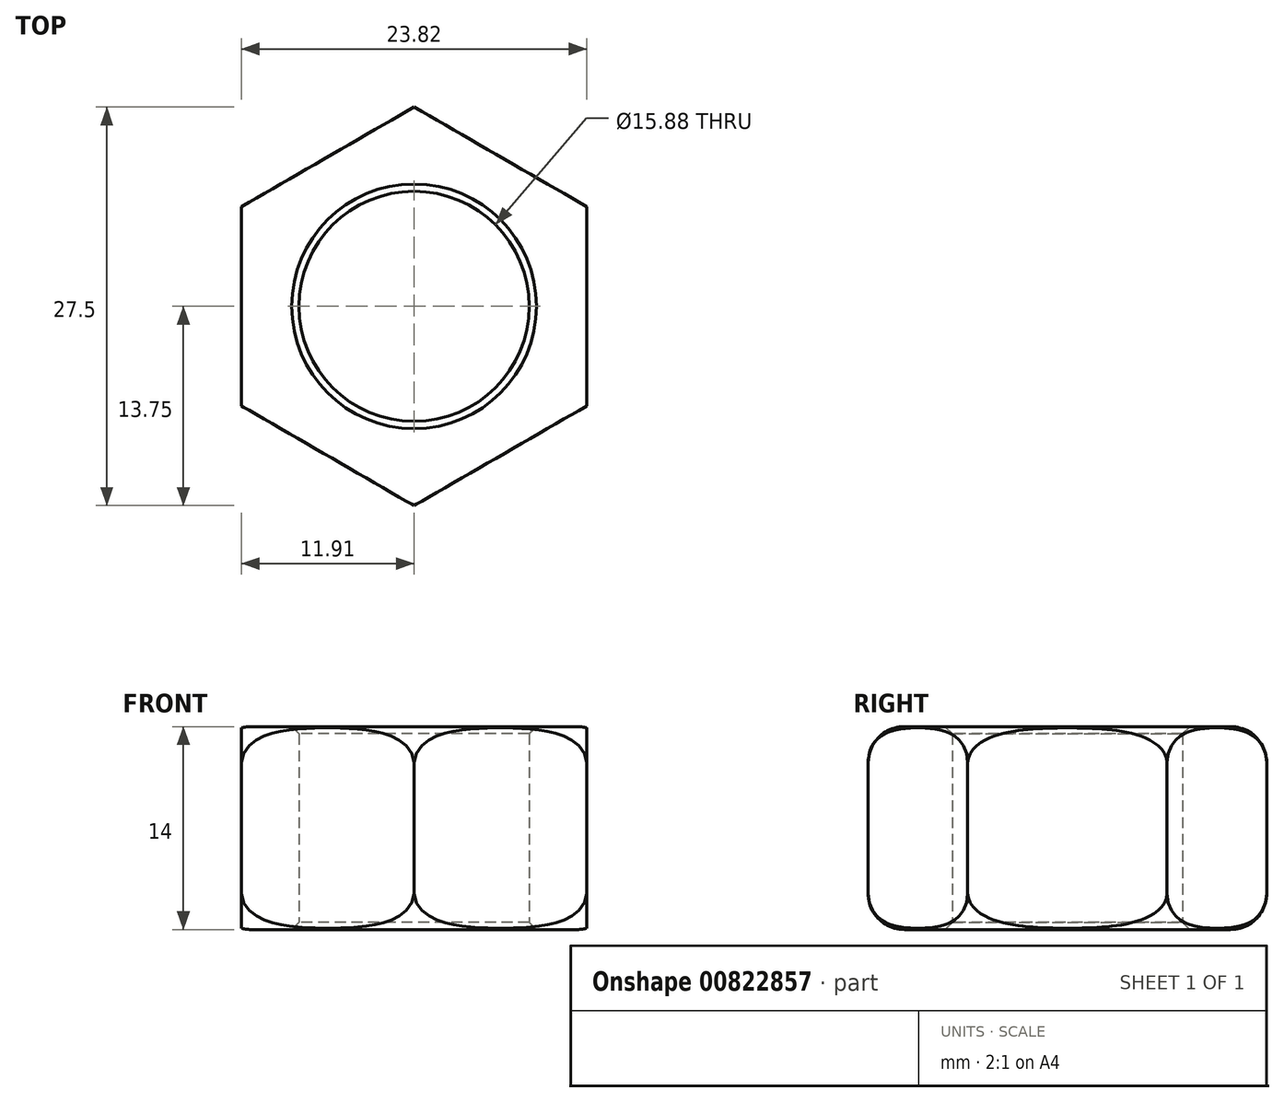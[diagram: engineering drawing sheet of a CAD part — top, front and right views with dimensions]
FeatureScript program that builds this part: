
annotation { "Feature Type Name" : "Feature", "Feature Type Description" : "" }
export const myFeature = defineFeature(function(context is Context, id is Id, definition is map)
    precondition{}
    {
        {
            var Q0;
            Q0=qCreatedBy(makeId("Top.planeOp"),FACE);
            var sketch = newSketch(context, id + "F0", { "sketchPlane" : qUnion([Q0])});
            skLineSegment(sketch, "E0", {"start": v(0, 0) * mm, "end": v(11.9, 0) * mm, "construction": true});
            skCircle(sketch, "E1.cCircle", {"center": v(0, 0) * mm, "radius": 11.9 * mm, "construction": true});
            skLineSegment(sketch, "E1.0", {"start": v(11.9, 6.87) * mm, "end": v(11.9, -6.87) * mm, "construction": true});
            skLineSegment(sketch, "E1.1", {"start": v(11.9, -6.87) * mm, "end": v(0, -13.75) * mm, "construction": true});
            skLineSegment(sketch, "E1.2", {"start": v(0, -13.75) * mm, "end": v(-11.9, -6.87) * mm, "construction": true});
            skLineSegment(sketch, "E1.3", {"start": v(-11.9, -6.87) * mm, "end": v(-11.9, 6.87) * mm, "construction": true});
            skLineSegment(sketch, "E1.4", {"start": v(-11.9, 6.87) * mm, "end": v(0, 13.75) * mm, "construction": true});
            skLineSegment(sketch, "E1.5", {"start": v(0, 13.75) * mm, "end": v(11.9, 6.87) * mm, "construction": true});
            skPoint(sketch, "E1.0.midPoint", {"position": v(11.9, 0) * mm});
            skCircle(sketch, "E2", {"center": v(0, 0) * mm, "radius": 13.75 * mm});
            skCircle(sketch, "E3", {"center": v(0, 0) * mm, "radius": 7.94 * mm});
            skSolve(sketch);
        }
        {
            var Q0;
            Q0 = qSketchRegion(id + "F0", true);
            extrude(context, id + "F1", {"entities" : qUnion([Q0]), "depth" : 14 * mm, "offsetDistance" : 25 * mm});
        }
        {
            var Q0;
            Q0=makeQuery(id+"F1.opExtrude","CAP_FACE",FACE,{"disambiguationData":[OSD([sQuery(id+"F0.wireOp",EDGE,"E2"),sQuery(id+"F0.wireOp",EDGE,"E3")])],"isStart":false});
            var sketch = newSketch(context, id + "F2", { "sketchPlane" : qUnion([Q0])});
            skLineSegment(sketch, "E4.0", {"start": v(0, 13.75) * mm, "end": v(11.9, 6.87) * mm});
            skLineSegment(sketch, "E5.0", {"start": v(-11.9, 6.87) * mm, "end": v(0, 13.75) * mm});
            skLineSegment(sketch, "E6.0", {"start": v(-11.9, -6.87) * mm, "end": v(-11.9, 6.87) * mm});
            skLineSegment(sketch, "E7.0", {"start": v(0, -13.75) * mm, "end": v(-11.9, -6.87) * mm});
            skLineSegment(sketch, "E8.0", {"start": v(11.9, -6.87) * mm, "end": v(0, -13.75) * mm});
            skLineSegment(sketch, "E9.0", {"start": v(11.9, 6.87) * mm, "end": v(11.9, -6.87) * mm});
            skCircle(sketch, "E10", {"center": v(0, 0) * mm, "radius": 16.81 * mm});
            skSolve(sketch);
        }
        {
            var Q0;
            Q0=makeQuery(id+"F1.opExtrude","CAP_EDGE",EDGE,{"disambiguationData":[OSD([sQuery(id+"F0.wireOp",EDGE,"E2")])],"isStart":false});
            var Q1;
            Q1=makeQuery(id+"F1.opExtrude","CAP_EDGE",EDGE,{"disambiguationData":[OSD([sQuery(id+"F0.wireOp",EDGE,"E2")])],"isStart":true});
            fillet(context, id + "F3", {"entities" : qUnion([Q0, Q1]), "radius" : 2.5 * mm, "tangentPropagation" : true, "allowEdgeOverflow" : false});
        }
        {
            var Q0;
            Q0 = qSketchRegion(id + "F2", true);
            extrude(context, id + "F4", {"entities" : qUnion([Q0]), "operationType" : NewBodyOperationType.REMOVE, "oppositeDirection" : true, "depth" : 25 * mm, "offsetDistance" : 25 * mm});
        }
        {
            var Q0;
            Q0=makeQuery(id+"F1.opExtrude","SWEPT_FACE",FACE,{"disambiguationData":[OSD([sQuery(id+"F0.wireOp",EDGE,"E3")])]});
            chamfer(context, id + "F5", {"entities" : qUnion([Q0]), "width" : 0.5 * mm, "tangentPropagation" : true});
        }
    });
